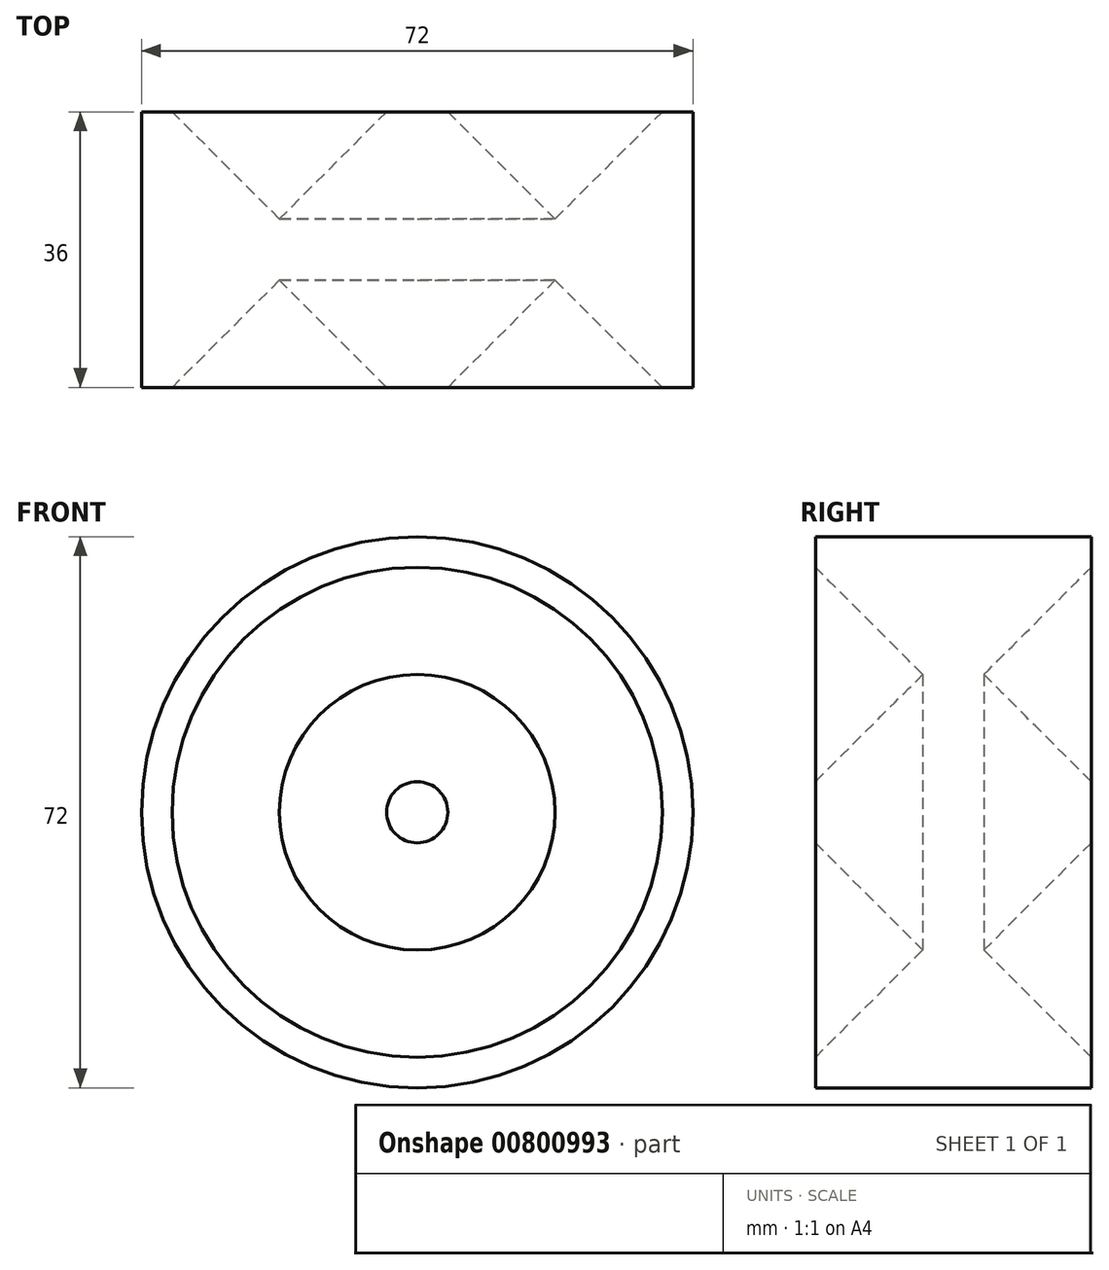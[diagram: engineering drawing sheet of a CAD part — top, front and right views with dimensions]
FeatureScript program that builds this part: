
annotation { "Feature Type Name" : "Feature", "Feature Type Description" : "" }
export const myFeature = defineFeature(function(context is Context, id is Id, definition is map)
    precondition{}
    {
        {
            var Q0;
            Q0=qCreatedBy(makeId("Top.planeOp"),FACE);
            var sketch = newSketch(context, id + "F0", { "sketchPlane" : qUnion([Q0])});
            skLineSegment(sketch, "E0", {"start": v(0, 0) * mm, "end": v(0, -36) * mm});
            skLineSegment(sketch, "E1", {"start": v(0, -36) * mm, "end": v(4, -36) * mm});
            skLineSegment(sketch, "E2", {"start": v(4, -36) * mm, "end": v(18, -22) * mm});
            skLineSegment(sketch, "E3", {"start": v(18, -22) * mm, "end": v(32, -36) * mm});
            skLineSegment(sketch, "E4", {"start": v(32, -36) * mm, "end": v(36, -36) * mm});
            skLineSegment(sketch, "E5", {"start": v(36, -36) * mm, "end": v(36, 0) * mm});
            skLineSegment(sketch, "E6", {"start": v(36, 0) * mm, "end": v(32, 0) * mm});
            skLineSegment(sketch, "E7", {"start": v(32, 0) * mm, "end": v(18, -14) * mm});
            skLineSegment(sketch, "E8", {"start": v(18, -14) * mm, "end": v(4, 0) * mm});
            skLineSegment(sketch, "E9", {"start": v(4, 0) * mm, "end": v(0, 0) * mm});
            skLineSegment(sketch, "E10", {"start": v(4, -30.34) * mm, "end": v(16.34, -18) * mm});
            skLineSegment(sketch, "E11", {"start": v(16.34, -18) * mm, "end": v(4, -5.66) * mm});
            skLineSegment(sketch, "E12", {"start": v(4, -5.66) * mm, "end": v(4, -30.34) * mm});
            skLineSegment(sketch, "E13", {"start": v(18, -14) * mm, "end": v(18, -22) * mm, "construction": true});
            skLineSegment(sketch, "E14.MirrorCS", {"start": v(19.66, -18) * mm, "end": v(32, -5.66) * mm});
            skLineSegment(sketch, "E15.MirrorCS", {"start": v(32, -5.66) * mm, "end": v(32, -30.34) * mm});
            skLineSegment(sketch, "E16.MirrorCS", {"start": v(32, -30.34) * mm, "end": v(19.66, -18) * mm});
            skSolve(sketch);
        }
        {
            var Q0;
            Q0=makeQuery(id+"F0.imprint","IMPRINT",FACE,{"disambiguationData":[TD([[makeQuery(id+"F0.imprint","IMPRINT",EDGE,{"derivedFrom":sQuery(id+"F0.wireOp",EDGE,"E0")}),1.0]])]});
            var Q1;
            Q1=makeQuery(id+"F0.imprint","IMPRINT",FACE,{"disambiguationData":[TD([[makeQuery(id+"F0.imprint","IMPRINT",EDGE,{"derivedFrom":sQuery(id+"F0.wireOp",EDGE,"E10")}),1.0]])]});
            var Q2;
            Q2=makeQuery(id+"F0.imprint","IMPRINT",FACE,{"disambiguationData":[TD([[makeQuery(id+"F0.imprint","IMPRINT",EDGE,{"derivedFrom":sQuery(id+"F0.wireOp",EDGE,"E14.MirrorCS")}),-1.0]])]});
            var Q3;
            Q3=sQuery(id+"F0.wireOp",EDGE,"E0");
            revolve(context, id + "F1", {"surfaceOperationType" : NewSurfaceOperationType.NEW, "entities" : qUnion([Q0, Q1, Q2]), "axis" : qUnion([Q3]), "revolveType" : RevolveType.FULL});
        }
    });
